# Revit family: Siedzisko_prysznicowe_uchylne_ze_wspornikami_stal_biała
name_source: partatom
category: Furniture
units: mm (PartAtom-declared; Revit-internal decimal feet)

## family parameters
Always vertical = Yes
Cut with Voids When Loaded = No
Host = Wall
Room Calculation Point = No
Shared = No

## types (1)
- S25KPUSWB
    Color / Kolor = Biały (white)
    Depth / Glebokosc = 460 mm  [stored 1.50919 ft]
    Description = Siedzisko prysznicowe uchylne ze wspornikami wykonane jest z odpornej na uszkodzenia stali węglowej. Białe wykończenie nadaje taboretowi łazienkowemu uniwersalny wygląd i sprawia, że można je łatwo wkomponować w różnorodne wnętrza. Krzesło toaletowe montuje się naściennie pod prysznicem w łazienkach dla osób niepełnosprawnych ruchowo. Ułatwia ono ludziom z problemami zdrowotnymi korzystanie z prysznica, zwiększając tym samym ich komfort i wygodę. Możliwość złożenia taboretu daje szasnę zaoszczędzić przestrzeń w czasie, gdy nie jest on użytkowany. Uniwersalne, solidne i wysoce funkcjonalne krzesełko gwarantuje dostosowanie toalety do potrzeb osób z dysfunkcjami ruchowymi.
    Height / Wysokosc = 200 mm  [stored 0.656168 ft]
    Manufacturer = FANECO.com
    Manufacturer code / Kod producenta = 5901764295303
    Material = Farba epoksydowa biała
    Material finish / Wykonczenie = Farba epoksydowa biała
    Product code / Kod produktu = S25KPUSWB
    Type Comments = Siedzisko prysznicowe uchylne ze wspornikami stal biała
    URL = https://faneco.com
    Weight / Waga = 7.2 kg
    Width / Szerokosc = 440 mm  [stored 1.44357 ft]

note: [stored X ft] marks values corroborated as IEEE doubles in the binary element streams (Revit-internal decimal feet)

## geometry (parser evidence)
native form markers: Sweep x11
no freeform markers — native parametric forms only
